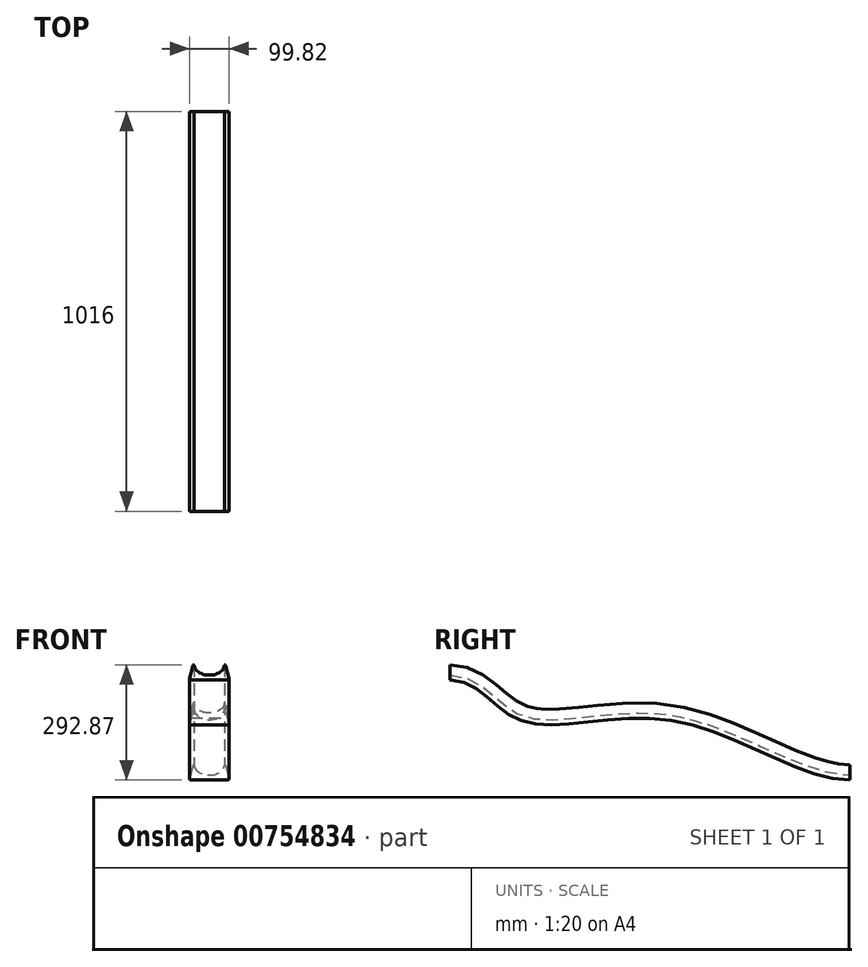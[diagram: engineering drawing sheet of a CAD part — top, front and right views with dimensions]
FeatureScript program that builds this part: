
annotation { "Feature Type Name" : "Feature", "Feature Type Description" : "" }
export const myFeature = defineFeature(function(context is Context, id is Id, definition is map)
    precondition{}
    {
        {
            var Q0;
            Q0=qCreatedBy(makeId("Front.planeOp"),FACE);
            var sketch = newSketch(context, id + "F0", { "sketchPlane" : qUnion([Q0])});
            skFitSpline(sketch, "E0", {"points": [v(-38.1, 0) * mm, v(38.1, 0) * mm], "startDerivative": vector(-38.1, -152.4) * mm, "endDerivative": vector(-38.1, 152.4) * mm});
            skLineSegment(sketch, "E1", {"start": v(-46.73, -50.8) * mm, "end": v(46.73, -50.8) * mm});
            skLineSegment(sketch, "E2", {"start": v(0, -50.8) * mm, "end": v(0, 0) * mm, "construction": true});
            skPoint(sketch, "E3", {"position": v(0, -50.8) * mm});
            skLineSegment(sketch, "E4", {"start": v(-41.32, -12.9) * mm, "end": v(-49.81, -46.85) * mm});
            skLineSegment(sketch, "E5", {"start": v(41.32, -12.9) * mm, "end": v(49.81, -46.85) * mm});
            skArc(sketch, "E6.filletArc", {"start": v(-38.84, -13) * mm, "mid": v(-40.04, -11.93) * mm, "end": v(-41.32, -12.9) * mm});
            skArc(sketch, "E7.filletArc", {"start": v(41.32, -12.9) * mm, "mid": v(40.04, -11.93) * mm, "end": v(38.84, -13) * mm});
            skArc(sketch, "E8.filletArc", {"start": v(-49.81, -46.85) * mm, "mid": v(-49.24, -49.58) * mm, "end": v(-46.73, -50.8) * mm});
            skArc(sketch, "E9.filletArc", {"start": v(46.73, -50.8) * mm, "mid": v(49.24, -49.58) * mm, "end": v(49.81, -46.85) * mm});
            skSolve(sketch);
        }
        {
            var Q0;
            Q0=qCreatedBy(makeId("Right.planeOp"),FACE);
            var sketch = newSketch(context, id + "F1", { "sketchPlane" : qUnion([Q0])});
            skFitSpline(sketch, "E10", {"points": [v(0, -50.8) * mm, v(177.8, -152.4) * mm, v(558.8, -152.4) * mm, v(1016, -304.8) * mm], "startDerivative": vector(891.1, 0) * mm, "endDerivative": vector(968.12, 0) * mm});
            skSolve(sketch);
        }
        {
            var Q0;
            Q0=makeQuery(id+"F0.imprint","IMPRINT",FACE,{"disambiguationData":[TD([[makeQuery(id+"F0.imprint","IMPRINT",EDGE,{"derivedFrom":sQuery(id+"F0.wireOp",EDGE,"E0")}),-1.0]])]});
            var Q1;
            Q1=sQuery(id+"F1.wireOp",EDGE,"E10");
            sweep(context, id + "F2", {"profiles" : qUnion([Q0]), "path" : qUnion([Q1])});
        }
    });
